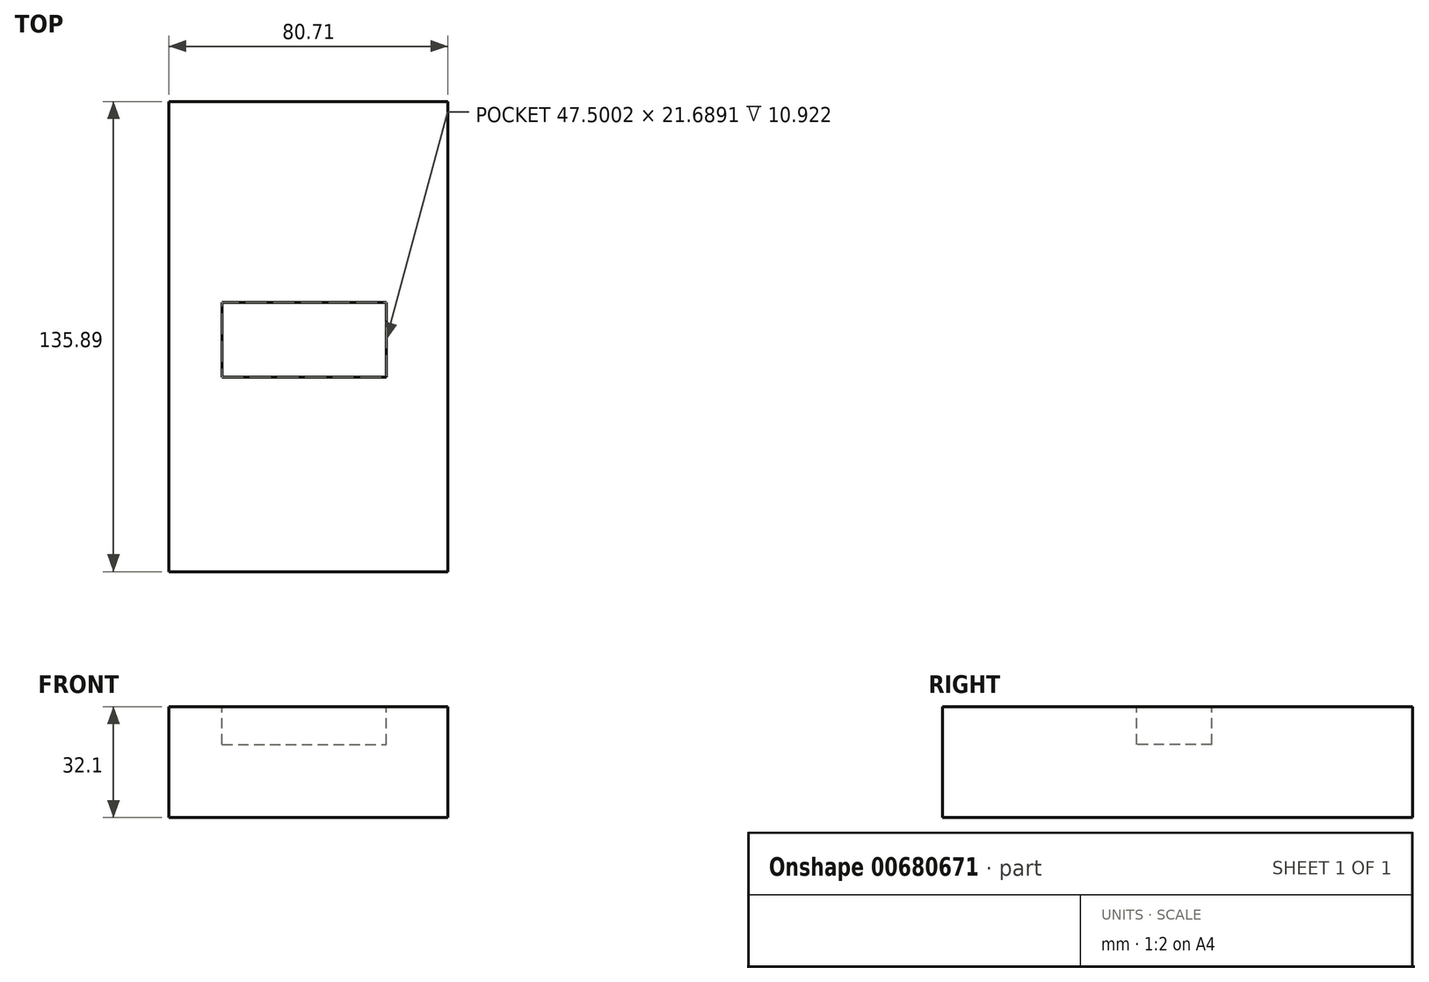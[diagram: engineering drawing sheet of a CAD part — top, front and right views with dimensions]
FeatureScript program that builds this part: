
annotation { "Feature Type Name" : "Feature", "Feature Type Description" : "" }
export const myFeature = defineFeature(function(context is Context, id is Id, definition is map)
    precondition{}
    {
        {
            var Q0;
            Q0=qCreatedBy(makeId("Front.planeOp"),FACE);
            var sketch = newSketch(context, id + "F0", { "sketchPlane" : qUnion([Q0])});
            skLineSegment(sketch, "E0", {"start": v(-131.67, 54.14) * mm, "end": v(-50.96, 54.14) * mm});
            skLineSegment(sketch, "E1", {"start": v(-50.96, 54.14) * mm, "end": v(-50.96, 22.04) * mm});
            skLineSegment(sketch, "E2", {"start": v(-50.96, 22.04) * mm, "end": v(-131.67, 22.04) * mm});
            skLineSegment(sketch, "E3", {"start": v(-131.67, 22.04) * mm, "end": v(-131.67, 54.14) * mm});
            skSolve(sketch);
        }
        {
            var Q0;
            Q0=makeQuery(id+"F0.imprint","IMPRINT",FACE,{"disambiguationData":[TD([[makeQuery(id+"F0.imprint","IMPRINT",EDGE,{"derivedFrom":sQuery(id+"F0.wireOp",EDGE,"E0")}),-1.0]])]});
            extrude(context, id + "F1", {"entities" : qUnion([Q0]), "depth" : 135.89 * mm, "offsetDistance" : 25.4 * mm});
        }
        {
            var Q0;
            Q0=makeQuery(id+"F1.opExtrude","SWEPT_FACE",FACE,{"disambiguationData":[OSD([sQuery(id+"F0.wireOp",EDGE,"E0")])]});
            var sketch = newSketch(context, id + "F2", { "sketchPlane" : qUnion([Q0])});
            skLineSegment(sketch, "E4.bottom", {"start": v(-116.23, -58.05) * mm, "end": v(-68.73, -58.05) * mm});
            skLineSegment(sketch, "E4.top", {"start": v(-116.23, -79.74) * mm, "end": v(-68.73, -79.74) * mm});
            skLineSegment(sketch, "E4.left", {"start": v(-116.23, -58.05) * mm, "end": v(-116.23, -79.74) * mm});
            skLineSegment(sketch, "E4.right", {"start": v(-68.73, -58.05) * mm, "end": v(-68.73, -79.74) * mm});
            skSolve(sketch);
        }
        {
            var Q0;
            Q0=makeQuery(id+"F2.imprint","IMPRINT",FACE,{"disambiguationData":[TD([[makeQuery(id+"F2.imprint","IMPRINT",EDGE,{"derivedFrom":sQuery(id+"F2.wireOp",EDGE,"E4.bottom")}),-1.0]])]});
            extrude(context, id + "F3", {"entities" : qUnion([Q0]), "operationType" : NewBodyOperationType.REMOVE, "oppositeDirection" : true, "depth" : 10.92 * mm, "offsetDistance" : 25.4 * mm});
        }
    });
